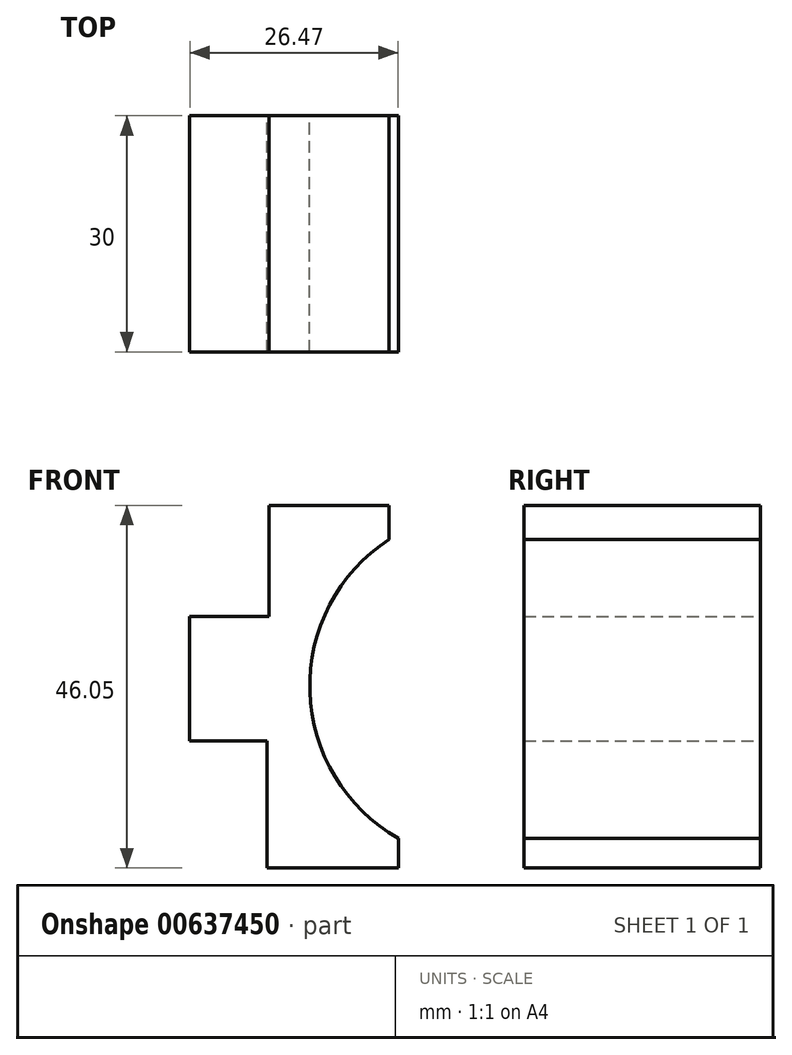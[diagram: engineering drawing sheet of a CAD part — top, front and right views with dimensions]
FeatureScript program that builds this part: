
annotation { "Feature Type Name" : "Feature", "Feature Type Description" : "" }
export const myFeature = defineFeature(function(context is Context, id is Id, definition is map)
    precondition{}
    {
        {
            var Q0;
            Q0=qCreatedBy(makeId("Front.planeOp"),FACE);
            var sketch = newSketch(context, id + "F0", { "sketchPlane" : qUnion([Q0])});
            skLineSegment(sketch, "E0", {"start": v(-30.65, 21.73) * mm, "end": v(-40.72, 21.73) * mm});
            skLineSegment(sketch, "E1", {"start": v(-40.72, 21.73) * mm, "end": v(-40.72, 5.9) * mm});
            skLineSegment(sketch, "E2", {"start": v(-40.72, 5.9) * mm, "end": v(-30.94, 5.9) * mm});
            skLineSegment(sketch, "E3", {"start": v(-30.94, 5.9) * mm, "end": v(-30.94, -10.22) * mm});
            skLineSegment(sketch, "E4", {"start": v(-30.94, -10.22) * mm, "end": v(-14.25, -10.22) * mm});
            skLineSegment(sketch, "E5", {"start": v(-14.25, -10.22) * mm, "end": v(-14.25, -6.48) * mm});
            skLineSegment(sketch, "E6", {"start": v(-30.65, 21.73) * mm, "end": v(-30.65, 35.83) * mm});
            skLineSegment(sketch, "E7", {"start": v(-30.65, 35.83) * mm, "end": v(-15.4, 35.83) * mm});
            skLineSegment(sketch, "E8", {"start": v(-15.4, 35.83) * mm, "end": v(-15.4, 31.51) * mm});
            skArc(sketch, "E9", {"start": v(-15.4, 31.51) * mm, "mid": v(-25.48, 12.2) * mm, "end": v(-14.25, -6.48) * mm});
            skSolve(sketch);
        }
        {
            var Q0;
            Q0 = qSketchRegion(id + "F0", true);
            extrude(context, id + "F1", {"entities" : qUnion([Q0]), "depth" : 30 * mm, "offsetDistance" : 25 * mm});
        }
    });
